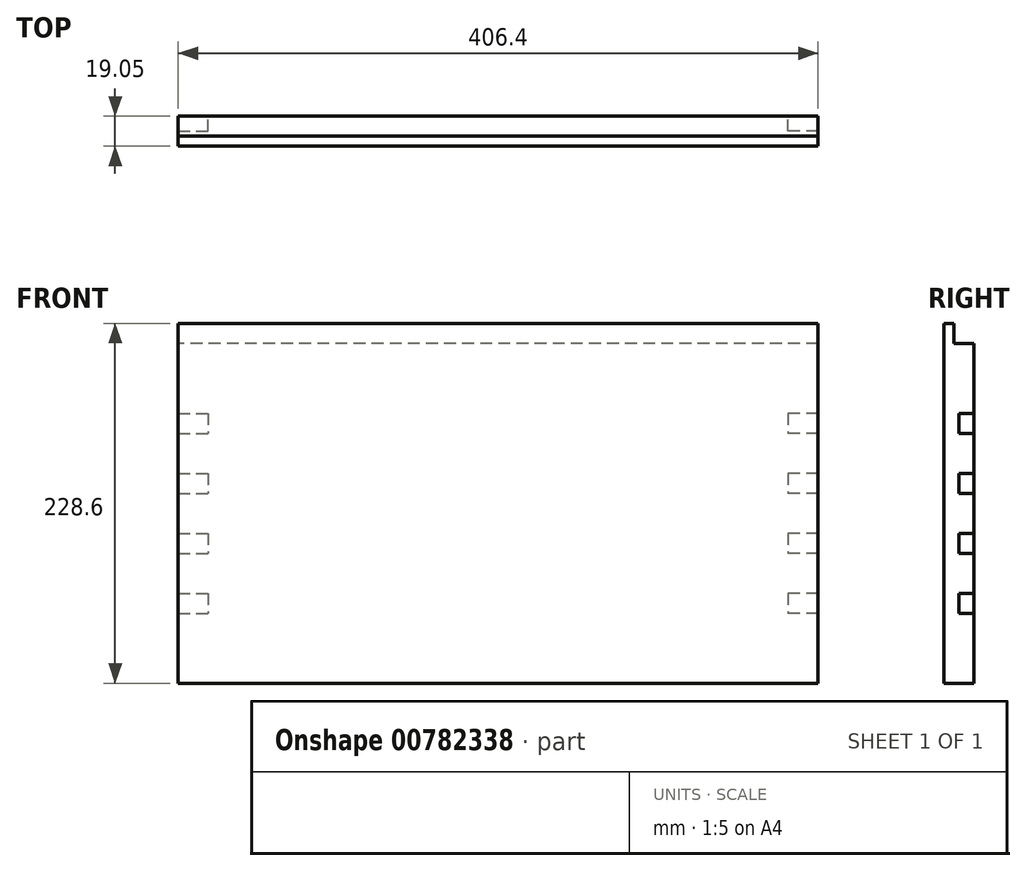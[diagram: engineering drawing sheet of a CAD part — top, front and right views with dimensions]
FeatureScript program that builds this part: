
annotation { "Feature Type Name" : "Feature", "Feature Type Description" : "" }
export const myFeature = defineFeature(function(context is Context, id is Id, definition is map)
    precondition{}
    {
        {
            var Q0;
            Q0=qCreatedBy(makeId("Front.planeOp"),FACE);
            var sketch = newSketch(context, id + "F0", { "sketchPlane" : qUnion([Q0])});
            skLineSegment(sketch, "E0.bottom", {"start": v(-203.2, -114.3) * mm, "end": v(203.2, -114.3) * mm});
            skLineSegment(sketch, "E0.top", {"start": v(-203.2, 114.3) * mm, "end": v(203.2, 114.3) * mm});
            skLineSegment(sketch, "E0.left", {"start": v(-203.2, -114.3) * mm, "end": v(-203.2, 114.3) * mm});
            skLineSegment(sketch, "E0.right", {"start": v(203.2, -114.3) * mm, "end": v(203.2, 114.3) * mm});
            skPoint(sketch, "E0.middle", {"position": v(0, 0) * mm});
            skSolve(sketch);
        }
        {
            var Q0;
            Q0=makeQuery(id+"F0.imprint","IMPRINT",FACE,{"disambiguationData":[TD([[makeQuery(id+"F0.imprint","IMPRINT",EDGE,{"derivedFrom":sQuery(id+"F0.wireOp",EDGE,"E0.bottom")}),1.0]])]});
            var Q1;
            Q1=sQuery(id+"F0.wireOp",EDGE,"E0.top");
            var Q2;
            Q2=sQuery(id+"F0.wireOp",EDGE,"E0.right");
            var Q3;
            Q3=sQuery(id+"F0.wireOp",EDGE,"E0.left");
            var Q4;
            Q4=sQuery(id+"F0.wireOp",EDGE,"E0.bottom");
            extrude(context, id + "F1", {"entities" : qUnion([Q0]), "surfaceEntities" : qUnion([Q1, Q2, Q3, Q4]), "depth" : 19.05 * mm, "offsetDistance" : 25.4 * mm});
        }
        {
            var Q0;
            Q0=makeQuery(id+"F1.opExtrude","SWEPT_FACE",FACE,{"disambiguationData":[OSD([sQuery(id+"F0.wireOp",EDGE,"E0.left")])]});
            var sketch = newSketch(context, id + "F2", { "sketchPlane" : qUnion([Q0])});
            skPoint(sketch, "E1.oppositeSnap0", {"position": v(12.7, 117.01) * mm});
            skLineSegment(sketch, "E1.bottom", {"start": v(0, 114.3) * mm, "end": v(12.7, 114.3) * mm});
            skLineSegment(sketch, "E1.top", {"start": v(0, 101.6) * mm, "end": v(12.7, 101.6) * mm});
            skLineSegment(sketch, "E1.left", {"start": v(0, 114.3) * mm, "end": v(0, 101.6) * mm});
            skLineSegment(sketch, "E1.right", {"start": v(12.7, 114.3) * mm, "end": v(12.7, 101.6) * mm});
            skSolve(sketch);
        }
        {
            var Q0;
            Q0=makeQuery(id+"F2.imprint","IMPRINT",FACE,{"disambiguationData":[TD([[makeQuery(id+"F2.imprint","IMPRINT",EDGE,{"derivedFrom":sQuery(id+"F2.wireOp",EDGE,"E1.bottom")}),1.0]])]});
            extrude(context, id + "F3", {"entities" : qUnion([Q0]), "operationType" : NewBodyOperationType.REMOVE, "endBound" : BoundingType.UP_TO_NEXT, "oppositeDirection" : true, "depth" : 25.4 * mm, "offsetDistance" : 25.4 * mm});
        }
        {
            var Q0;
            Q0=makeQuery(id+"F1.opExtrude","CAP_FACE",FACE,{"disambiguationData":[OSD([sQuery(id+"F0.wireOp",EDGE,"E0.bottom"),sQuery(id+"F0.wireOp",EDGE,"E0.top"),sQuery(id+"F0.wireOp",EDGE,"E0.left"),sQuery(id+"F0.wireOp",EDGE,"E0.right")])],"isStart":true});
            var sketch = newSketch(context, id + "F4", { "sketchPlane" : qUnion([Q0])});
            skLineSegment(sketch, "E2", {"start": v(0, 101.6) * mm, "end": v(0, -114.3) * mm, "construction": true});
            skLineSegment(sketch, "E3", {"start": v(-203.2, 0) * mm, "end": v(203.2, 0) * mm});
            skLineSegment(sketch, "E4.bottom", {"start": v(-203.2, 57.15) * mm, "end": v(-184.15, 57.15) * mm});
            skLineSegment(sketch, "E4.top", {"start": v(-203.2, 44.45) * mm, "end": v(-184.15, 44.45) * mm});
            skLineSegment(sketch, "E4.left", {"start": v(-203.2, 57.15) * mm, "end": v(-203.2, 44.45) * mm});
            skLineSegment(sketch, "E4.right", {"start": v(-184.15, 57.15) * mm, "end": v(-184.15, 44.45) * mm});
            skLineSegment(sketch, "E5.bottom", {"start": v(-203.2, 19.05) * mm, "end": v(-184.15, 19.05) * mm});
            skLineSegment(sketch, "E5.top", {"start": v(-203.2, 6.35) * mm, "end": v(-184.15, 6.35) * mm});
            skLineSegment(sketch, "E5.left", {"start": v(-203.2, 19.05) * mm, "end": v(-203.2, 6.35) * mm});
            skLineSegment(sketch, "E5.right", {"start": v(-184.15, 19.05) * mm, "end": v(-184.15, 6.35) * mm});
            skLineSegment(sketch, "E6.bottom", {"start": v(-203.2, -19.05) * mm, "end": v(-184.15, -19.05) * mm});
            skLineSegment(sketch, "E6.top", {"start": v(-203.2, -31.75) * mm, "end": v(-184.15, -31.75) * mm});
            skLineSegment(sketch, "E6.left", {"start": v(-203.2, -19.05) * mm, "end": v(-203.2, -31.75) * mm});
            skLineSegment(sketch, "E6.right", {"start": v(-184.15, -19.05) * mm, "end": v(-184.15, -31.75) * mm});
            skLineSegment(sketch, "E7.bottom", {"start": v(-203.2, -57.15) * mm, "end": v(-184.15, -57.15) * mm});
            skLineSegment(sketch, "E7.top", {"start": v(-203.2, -69.85) * mm, "end": v(-184.15, -69.85) * mm});
            skLineSegment(sketch, "E7.left", {"start": v(-203.2, -57.15) * mm, "end": v(-203.2, -69.85) * mm});
            skLineSegment(sketch, "E7.right", {"start": v(-184.15, -57.15) * mm, "end": v(-184.15, -69.85) * mm});
            skLineSegment(sketch, "E8.MirrorCS", {"start": v(184.15, 57.15) * mm, "end": v(184.15, 44.45) * mm});
            skLineSegment(sketch, "E9.MirrorCS", {"start": v(203.2, 57.15) * mm, "end": v(184.15, 57.15) * mm});
            skLineSegment(sketch, "E10.MirrorCS", {"start": v(203.2, 57.15) * mm, "end": v(203.2, 44.45) * mm});
            skLineSegment(sketch, "E11.MirrorCS", {"start": v(203.2, 44.45) * mm, "end": v(184.15, 44.45) * mm});
            skLineSegment(sketch, "E12.MirrorCS", {"start": v(203.2, 19.05) * mm, "end": v(184.15, 19.05) * mm});
            skLineSegment(sketch, "E13.MirrorCS", {"start": v(184.15, 19.05) * mm, "end": v(184.15, 6.35) * mm});
            skLineSegment(sketch, "E14.MirrorCS", {"start": v(203.2, 6.35) * mm, "end": v(184.15, 6.35) * mm});
            skLineSegment(sketch, "E15.MirrorCS", {"start": v(203.2, 19.05) * mm, "end": v(203.2, 6.35) * mm});
            skLineSegment(sketch, "E16.MirrorCS", {"start": v(203.2, -19.05) * mm, "end": v(184.15, -19.05) * mm});
            skLineSegment(sketch, "E17.MirrorCS", {"start": v(203.2, -19.05) * mm, "end": v(203.2, -31.75) * mm});
            skLineSegment(sketch, "E18.MirrorCS", {"start": v(203.2, -31.75) * mm, "end": v(184.15, -31.75) * mm});
            skLineSegment(sketch, "E19.MirrorCS", {"start": v(184.15, -19.05) * mm, "end": v(184.15, -31.75) * mm});
            skLineSegment(sketch, "E20.MirrorCS", {"start": v(203.2, -57.15) * mm, "end": v(203.2, -69.85) * mm});
            skLineSegment(sketch, "E21.MirrorCS", {"start": v(203.2, -57.15) * mm, "end": v(184.15, -57.15) * mm});
            skLineSegment(sketch, "E22.MirrorCS", {"start": v(184.15, -57.15) * mm, "end": v(184.15, -69.85) * mm});
            skLineSegment(sketch, "E23.MirrorCS", {"start": v(203.2, -69.85) * mm, "end": v(184.15, -69.85) * mm});
            skSolve(sketch);
        }
        {
            var Q0;
            Q0=qSketchRegion(id+"F4",true);
            extrude(context, id + "F5", {"entities" : qUnion([Q0]), "operationType" : NewBodyOperationType.REMOVE, "oppositeDirection" : true, "depth" : 9.52 * mm, "offsetDistance" : 25.4 * mm});
        }
    });
